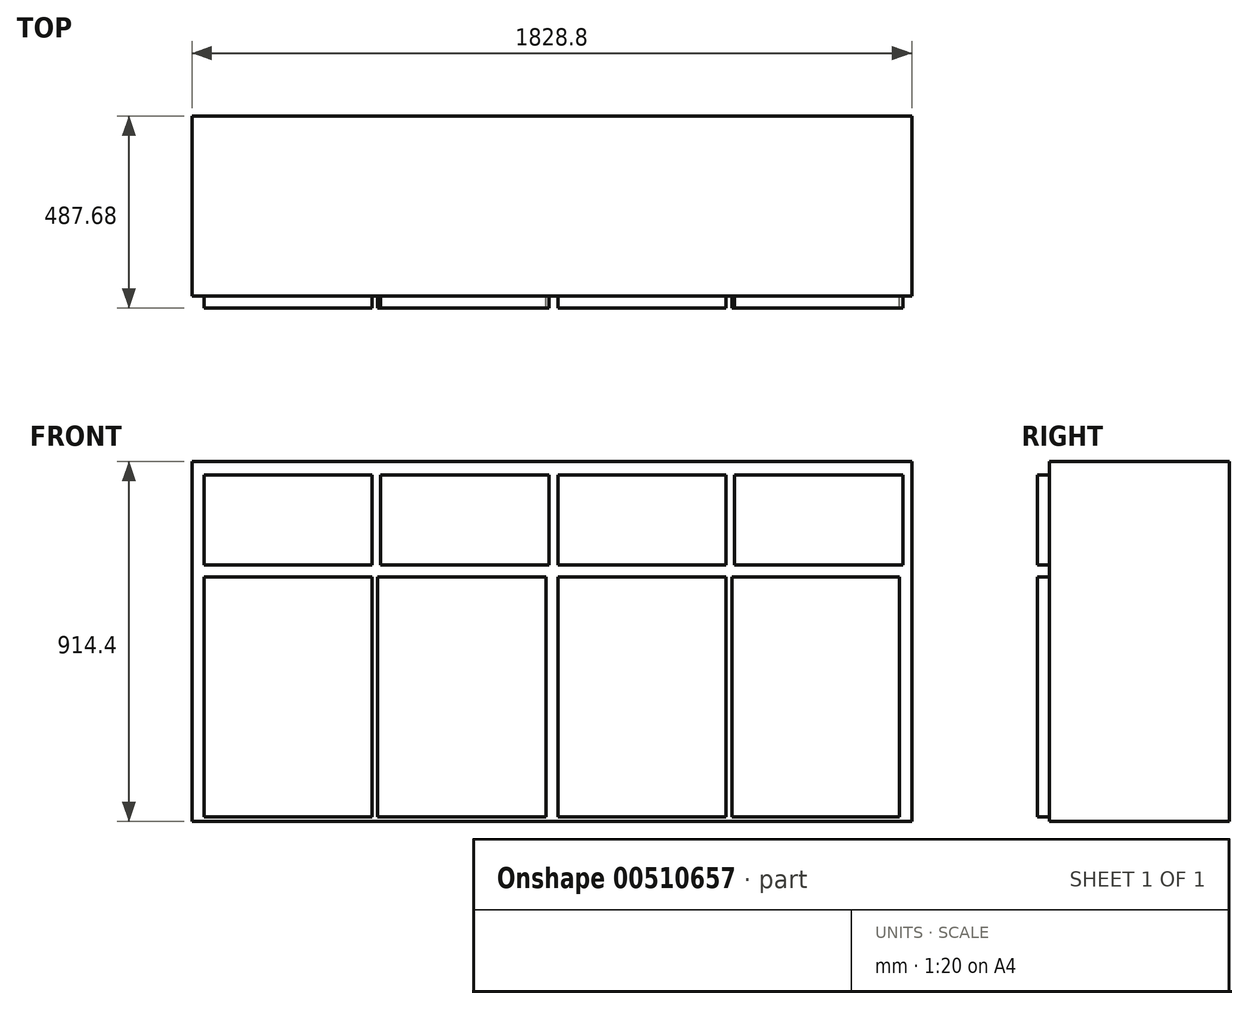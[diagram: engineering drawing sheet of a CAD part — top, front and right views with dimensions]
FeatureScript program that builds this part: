
annotation { "Feature Type Name" : "Feature", "Feature Type Description" : "" }
export const myFeature = defineFeature(function(context is Context, id is Id, definition is map)
    precondition{}
    {
        {
            var Q0;
            Q0=qCreatedBy(makeId("Top.planeOp"),FACE);
            var sketch = newSketch(context, id + "F0", { "sketchPlane" : qUnion([Q0])});
            skLineSegment(sketch, "E0.bottom", {"start": v(-917.25, 283.29) * mm, "end": v(911.55, 283.29) * mm});
            skLineSegment(sketch, "E0.top", {"start": v(-917.25, -173.91) * mm, "end": v(911.55, -173.91) * mm});
            skLineSegment(sketch, "E0.left", {"start": v(-917.25, 283.29) * mm, "end": v(-917.25, -173.91) * mm});
            skLineSegment(sketch, "E0.right", {"start": v(911.55, 283.29) * mm, "end": v(911.55, -173.91) * mm});
            skSolve(sketch);
        }
        {
            var Q0;
            Q0 = qSketchRegion(id + "F0", true);
            extrude(context, id + "F1", {"entities" : qUnion([Q0]), "depth" : 914.4 * mm, "offsetDistance" : 30.48 * mm});
        }
        {
            var Q0;
            Q0=makeQuery(id+"F1.opExtrude","SWEPT_FACE",FACE,{"disambiguationData":[OSD([sQuery(id+"F0.wireOp",EDGE,"E0.top")])]});
            var sketch = newSketch(context, id + "F2", { "sketchPlane" : qUnion([Q0])});
            skLineSegment(sketch, "E1.bottom", {"start": v(-886.77, 620.74) * mm, "end": v(-460.05, 620.74) * mm});
            skLineSegment(sketch, "E1.top", {"start": v(-886.77, 11.14) * mm, "end": v(-460.05, 11.14) * mm});
            skLineSegment(sketch, "E1.left", {"start": v(-886.77, 620.74) * mm, "end": v(-886.77, 11.14) * mm});
            skLineSegment(sketch, "E1.right", {"start": v(-460.05, 620.74) * mm, "end": v(-460.05, 11.14) * mm});
            skLineSegment(sketch, "E2.bottom", {"start": v(-444.8, 620.74) * mm, "end": v(-18.09, 620.74) * mm});
            skLineSegment(sketch, "E2.top", {"start": v(-444.8, 11.14) * mm, "end": v(-18.09, 11.14) * mm});
            skLineSegment(sketch, "E2.left", {"start": v(-444.8, 620.74) * mm, "end": v(-444.8, 11.14) * mm});
            skLineSegment(sketch, "E2.right", {"start": v(-18.09, 620.74) * mm, "end": v(-18.09, 11.14) * mm});
            skLineSegment(sketch, "E3.bottom", {"start": v(12.4, 620.74) * mm, "end": v(439.11, 620.74) * mm});
            skLineSegment(sketch, "E3.top", {"start": v(12.4, 11.14) * mm, "end": v(439.11, 11.14) * mm});
            skLineSegment(sketch, "E3.left", {"start": v(12.4, 620.74) * mm, "end": v(12.4, 11.14) * mm});
            skLineSegment(sketch, "E3.right", {"start": v(439.11, 620.74) * mm, "end": v(439.11, 11.14) * mm});
            skLineSegment(sketch, "E4.bottom", {"start": v(454.35, 620.74) * mm, "end": v(881.07, 620.74) * mm});
            skLineSegment(sketch, "E4.top", {"start": v(454.35, 11.14) * mm, "end": v(881.07, 11.14) * mm});
            skLineSegment(sketch, "E4.left", {"start": v(454.35, 620.74) * mm, "end": v(454.35, 11.14) * mm});
            skLineSegment(sketch, "E4.right", {"start": v(881.07, 620.74) * mm, "end": v(881.07, 11.14) * mm});
            skLineSegment(sketch, "E5.bottom", {"start": v(-886.77, 879.82) * mm, "end": v(-460.05, 879.82) * mm});
            skLineSegment(sketch, "E5.top", {"start": v(-886.77, 651.22) * mm, "end": v(-460.05, 651.22) * mm});
            skLineSegment(sketch, "E5.left", {"start": v(-886.77, 879.82) * mm, "end": v(-886.77, 651.22) * mm});
            skLineSegment(sketch, "E5.right", {"start": v(-460.05, 879.82) * mm, "end": v(-460.05, 651.22) * mm});
            skLineSegment(sketch, "E6.bottom", {"start": v(-437.19, 879.82) * mm, "end": v(-10.47, 879.82) * mm});
            skLineSegment(sketch, "E6.top", {"start": v(-437.19, 651.22) * mm, "end": v(-10.47, 651.22) * mm});
            skLineSegment(sketch, "E6.left", {"start": v(-437.19, 879.82) * mm, "end": v(-437.19, 651.22) * mm});
            skLineSegment(sketch, "E6.right", {"start": v(-10.47, 879.82) * mm, "end": v(-10.47, 651.22) * mm});
            skLineSegment(sketch, "E7.bottom", {"start": v(12.4, 879.82) * mm, "end": v(439.11, 879.82) * mm});
            skLineSegment(sketch, "E7.top", {"start": v(12.4, 651.22) * mm, "end": v(439.11, 651.22) * mm});
            skLineSegment(sketch, "E7.left", {"start": v(12.4, 879.82) * mm, "end": v(12.4, 651.22) * mm});
            skLineSegment(sketch, "E7.right", {"start": v(439.11, 879.82) * mm, "end": v(439.11, 651.22) * mm});
            skLineSegment(sketch, "E8.bottom", {"start": v(461.97, 879.82) * mm, "end": v(888.7, 879.82) * mm});
            skLineSegment(sketch, "E8.top", {"start": v(461.97, 651.22) * mm, "end": v(888.7, 651.22) * mm});
            skLineSegment(sketch, "E8.left", {"start": v(461.97, 879.82) * mm, "end": v(461.97, 651.22) * mm});
            skLineSegment(sketch, "E8.right", {"start": v(888.7, 879.82) * mm, "end": v(888.7, 651.22) * mm});
            skSolve(sketch);
        }
        {
            var Q0;
            Q0 = qSketchRegion(id + "F2", true);
            extrude(context, id + "F3", {"entities" : qUnion([Q0]), "operationType" : NewBodyOperationType.ADD, "depth" : 30.48 * mm, "offsetDistance" : 30.48 * mm});
        }
    });
